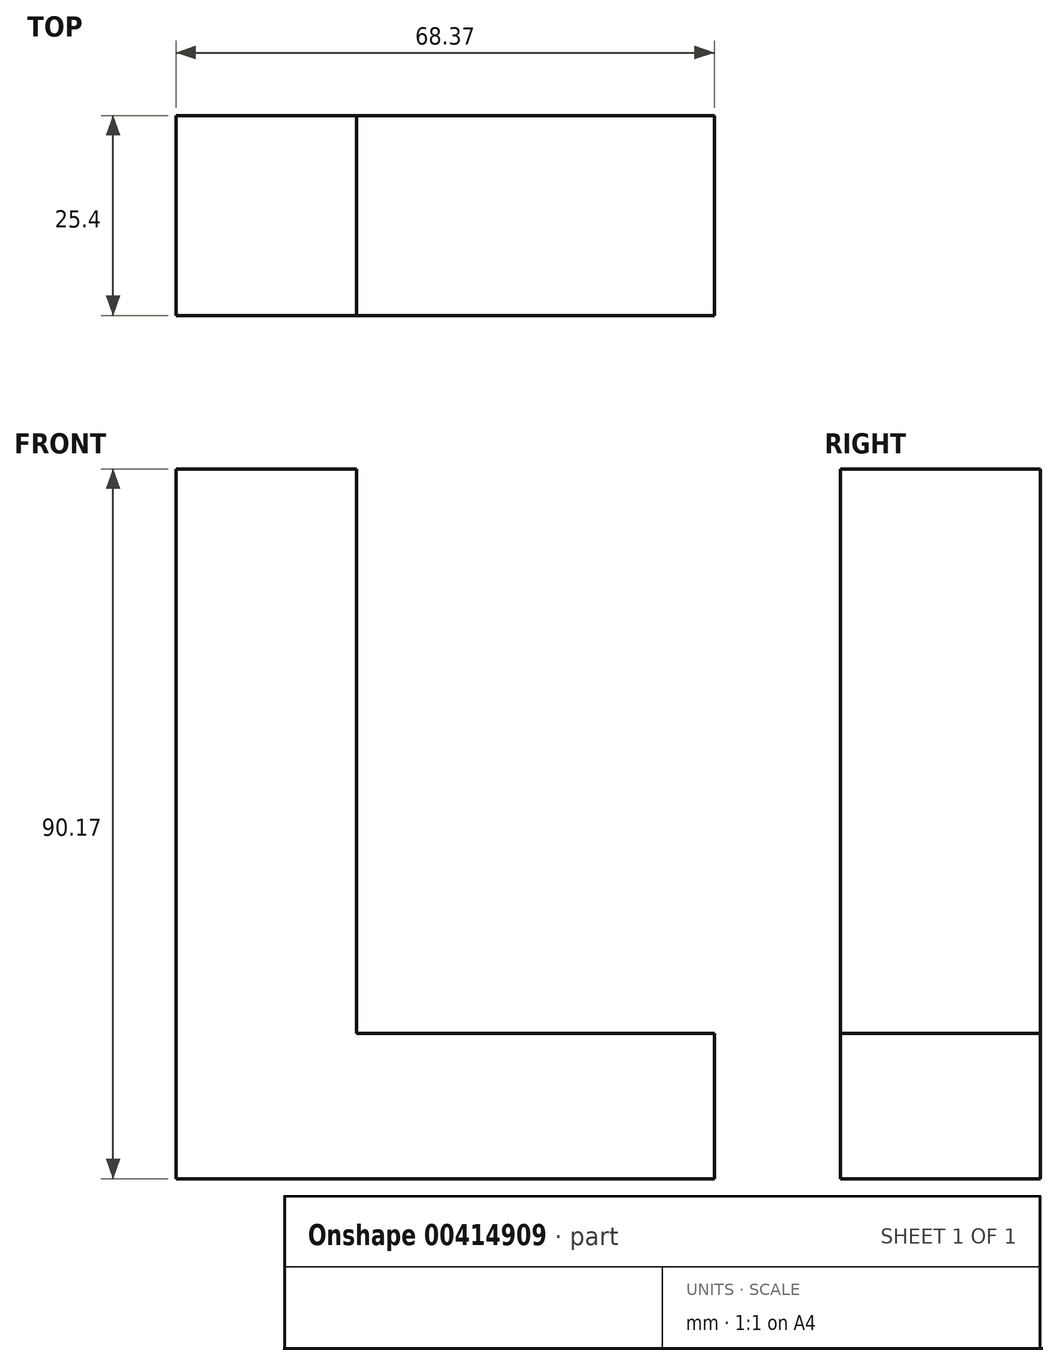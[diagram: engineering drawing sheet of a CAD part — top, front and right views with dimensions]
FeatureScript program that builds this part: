
annotation { "Feature Type Name" : "Feature", "Feature Type Description" : "" }
export const myFeature = defineFeature(function(context is Context, id is Id, definition is map)
    precondition{}
    {
        {
            var Q0;
            Q0=qCreatedBy(makeId("Front.planeOp"),FACE);
            var sketch = newSketch(context, id + "F0", { "sketchPlane" : qUnion([Q0])});
            skLineSegment(sketch, "E0", {"start": v(-42.5, 39.17) * mm, "end": v(-42.5, -51) * mm});
            skLineSegment(sketch, "E1", {"start": v(-42.5, -51) * mm, "end": v(25.87, -51) * mm});
            skLineSegment(sketch, "E2", {"start": v(25.87, -51) * mm, "end": v(25.87, -32.52) * mm});
            skLineSegment(sketch, "E3", {"start": v(25.87, -32.52) * mm, "end": v(-19.59, -32.52) * mm});
            skLineSegment(sketch, "E4", {"start": v(-19.59, -32.52) * mm, "end": v(-19.59, 39.17) * mm});
            skLineSegment(sketch, "E5", {"start": v(-19.59, 39.17) * mm, "end": v(-42.5, 39.17) * mm});
            skSolve(sketch);
        }
        {
            var Q0;
            Q0=makeQuery(id+"F0.imprint","IMPRINT",FACE,{"disambiguationData":[TD([[makeQuery(id+"F0.imprint","IMPRINT",EDGE,{"derivedFrom":sQuery(id+"F0.wireOp",EDGE,"E0")}),1.0]])]});
            extrude(context, id + "F1", {"entities" : qUnion([Q0]), "depth" : 25.4 * mm});
        }
    });
